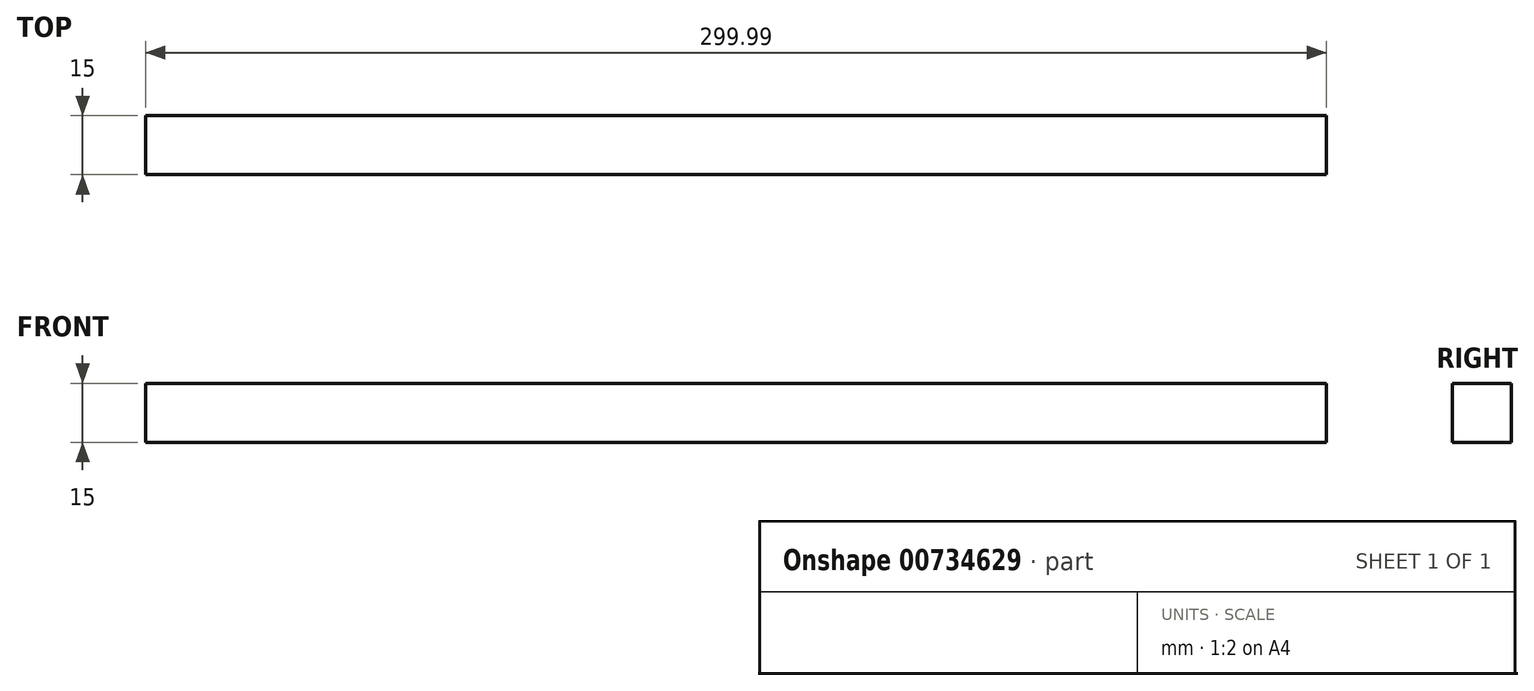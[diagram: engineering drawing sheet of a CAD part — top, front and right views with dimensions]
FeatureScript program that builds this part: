
annotation { "Feature Type Name" : "Feature", "Feature Type Description" : "" }
export const myFeature = defineFeature(function(context is Context, id is Id, definition is map)
    precondition{}
    {
        {
            var Q0;
            Q0=qCreatedBy(makeId("Front.planeOp"),FACE);
            var sketch = newSketch(context, id + "F0", { "sketchPlane" : qUnion([Q0])});
            skLineSegment(sketch, "E0", {"start": v(-150.56, 14.4) * mm, "end": v(149.43, 14.4) * mm});
            skLineSegment(sketch, "E1.0", {"start": v(-150.56, 29.4) * mm, "end": v(149.43, 29.4) * mm});
            skLineSegment(sketch, "E2", {"start": v(-150.56, 29.4) * mm, "end": v(-150.56, 14.4) * mm});
            skLineSegment(sketch, "E3", {"start": v(149.43, 29.4) * mm, "end": v(149.43, 14.4) * mm});
            skSolve(sketch);
        }
        {
            var Q0;
            Q0 = qSketchRegion(id + "F0", true);
            extrude(context, id + "F1", {"entities" : qUnion([Q0]), "depth" : 15 * mm, "offsetDistance" : 25 * mm});
        }
    });
